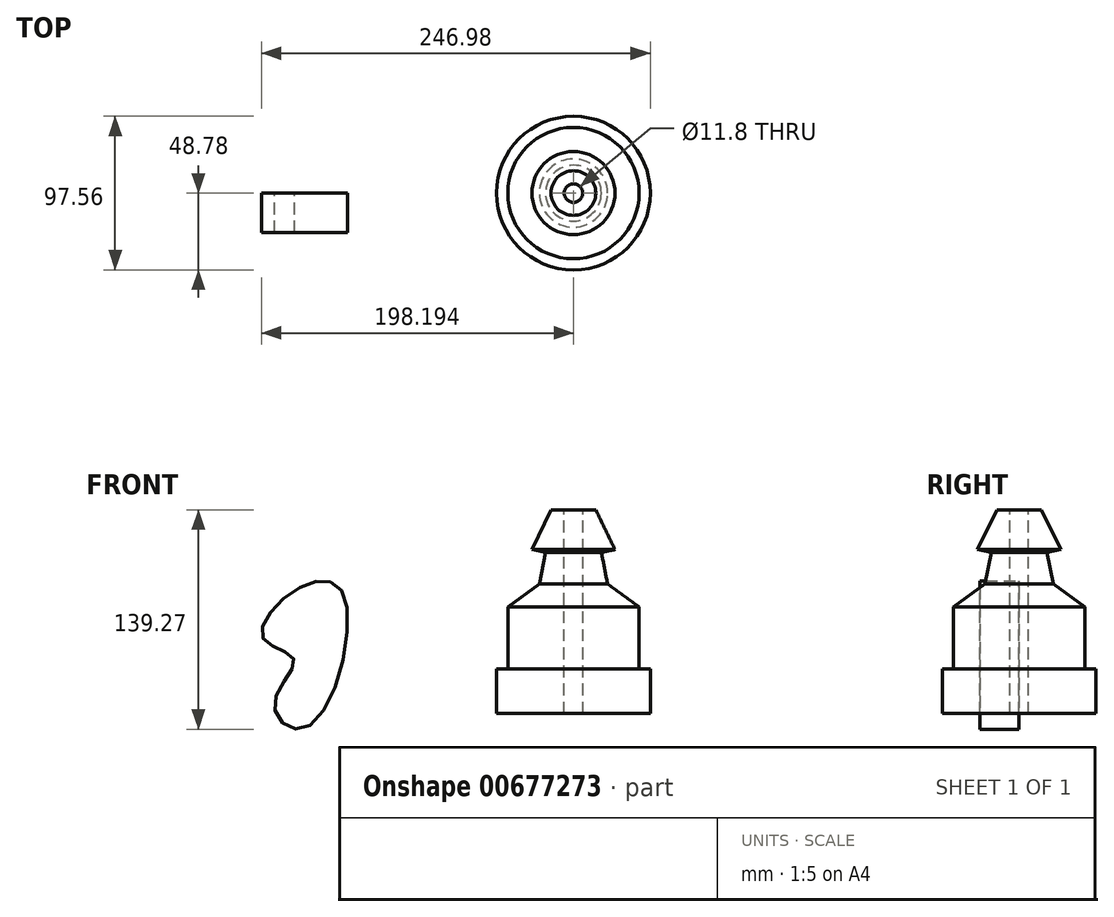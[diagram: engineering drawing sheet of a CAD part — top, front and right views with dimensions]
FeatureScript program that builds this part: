
annotation { "Feature Type Name" : "Feature", "Feature Type Description" : "" }
export const myFeature = defineFeature(function(context is Context, id is Id, definition is map)
    precondition{}
    {
        {
            var Q0;
            Q0=qCreatedBy(makeId("Front.planeOp"),FACE);
            var sketch = newSketch(context, id + "F0", { "sketchPlane" : qUnion([Q0])});
            skLineSegment(sketch, "E0", {"start": v(94.66, 81.3) * mm, "end": v(94.66, -11.55) * mm});
            skLineSegment(sketch, "E1", {"start": v(94.66, -11.55) * mm, "end": v(133.59, -11.55) * mm});
            skLineSegment(sketch, "E2", {"start": v(133.59, -11.55) * mm, "end": v(133.59, 0) * mm});
            skLineSegment(sketch, "E3", {"start": v(133.59, 0) * mm, "end": v(111.18, 0) * mm});
            skLineSegment(sketch, "E4", {"start": v(111.18, 0) * mm, "end": v(126.51, 0) * mm});
            skLineSegment(sketch, "E5", {"start": v(126.51, 0) * mm, "end": v(126.51, 39.54) * mm});
            skLineSegment(sketch, "E6", {"start": v(126.51, 39.54) * mm, "end": v(106.46, 54.04) * mm});
            skLineSegment(sketch, "E7", {"start": v(106.46, 54.04) * mm, "end": v(102.53, 74.13) * mm});
            skLineSegment(sketch, "E8", {"start": v(102.53, 74.13) * mm, "end": v(111.18, 75.83) * mm});
            skLineSegment(sketch, "E9", {"start": v(111.18, 75.83) * mm, "end": v(98.99, 101.03) * mm});
            skLineSegment(sketch, "E10", {"start": v(98.99, 101.03) * mm, "end": v(90.7, 101.03) * mm});
            skLineSegment(sketch, "E11", {"start": v(90.7, 101.03) * mm, "end": v(90.7, -28.27) * mm});
            skLineSegment(sketch, "E12", {"start": v(90.7, -28.27) * mm, "end": v(133.59, -28.27) * mm});
            skLineSegment(sketch, "E13", {"start": v(133.59, -28.27) * mm, "end": v(133.59, -11.55) * mm});
            skLineSegment(sketch, "E14", {"start": v(84.8, 101.64) * mm, "end": v(84.8, -41.37) * mm});
            skSolve(sketch);
        }
        {
            var Q0;
            Q0=makeQuery(id+"F0.imprint","IMPRINT",FACE,{"disambiguationData":[TD([[makeQuery(id+"F0.imprint","IMPRINT",EDGE,{"derivedFrom":sQuery(id+"F0.wireOp",EDGE,"E2")}),1.0]])]});
            var Q1;
            Q1=sQuery(id+"F0.wireOp",EDGE,"E14");
            revolve(context, id + "F1", {"entities" : qUnion([Q0]), "axis" : qUnion([Q1]), "revolveType" : RevolveType.FULL});
        }
        {
            var Q0;
            Q0=qCreatedBy(makeId("Front.planeOp"),FACE);
            var sketch = newSketch(context, id + "F2", { "sketchPlane" : qUnion([Q0])});
            skFitSpline(sketch, "E15", {"points": [v(-88.94, 51.79) * mm, v(-112.57, 19.65) * mm, v(-92.65, 6.16) * mm, v(-105.14, -22.76) * mm, v(-84.55, -37.07) * mm, v(-60.92, 46.71) * mm, v(-88.94, 51.79) * mm]});
            skSolve(sketch);
        }
        {
            var Q0;
            Q0=makeQuery(id+"F2.imprint","IMPRINT",FACE,{"disambiguationData":[TD([[makeQuery(id+"F2.imprint","IMPRINT",EDGE,{"derivedFrom":sQuery(id+"F2.wireOp",EDGE,"E15")}),1.0]])]});
            extrude(context, id + "F3", {"entities" : qUnion([Q0]), "depth" : 25 * mm, "offsetDistance" : 25 * mm});
        }
    });
